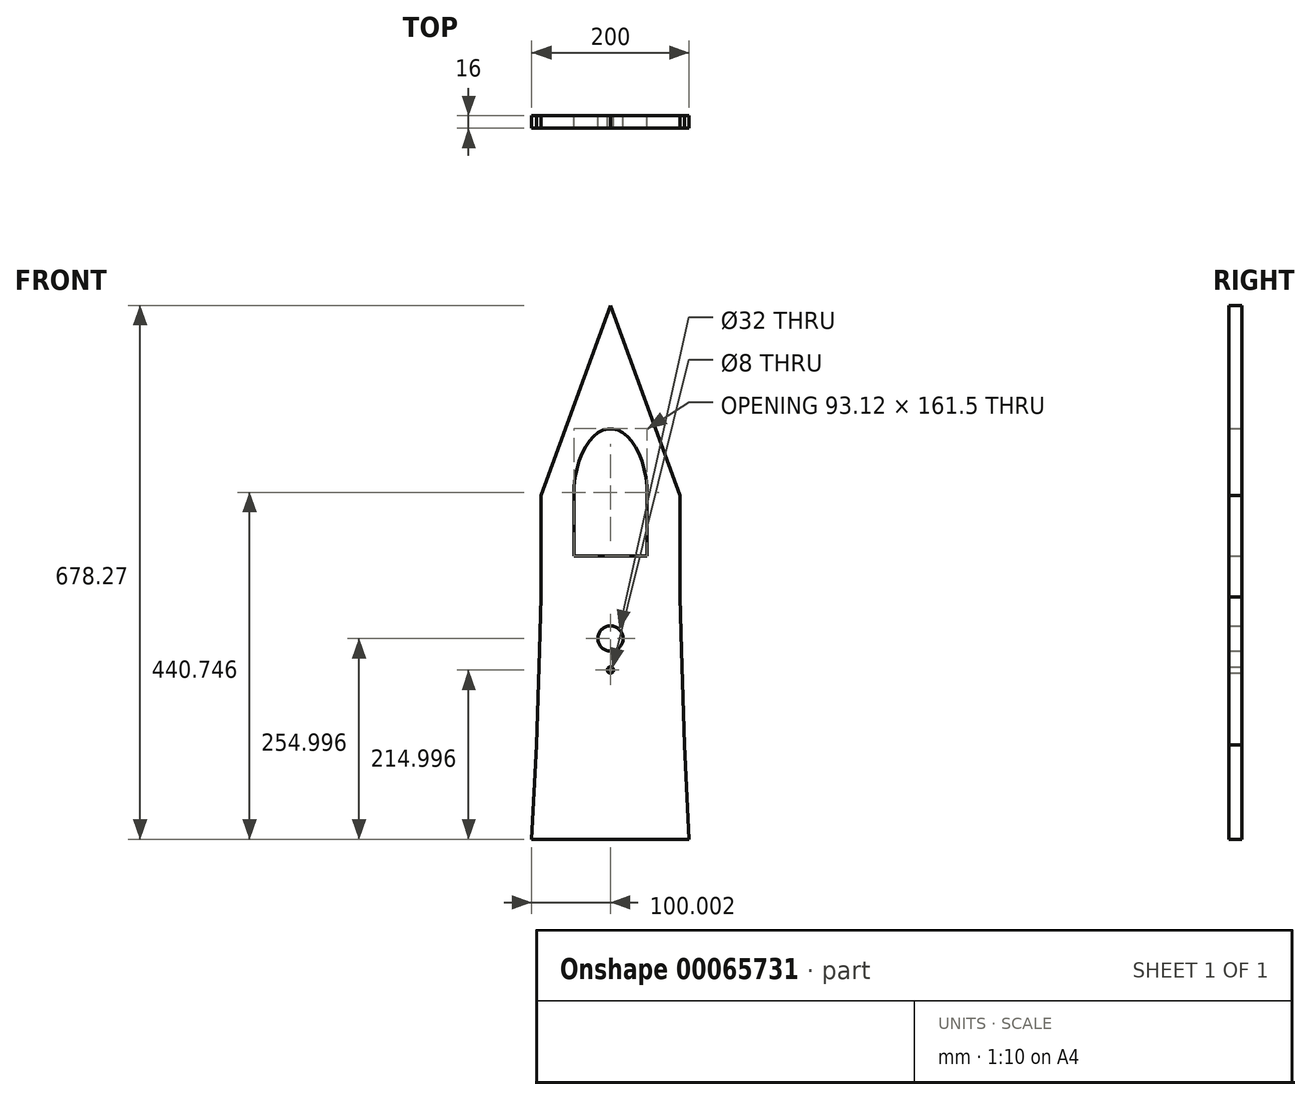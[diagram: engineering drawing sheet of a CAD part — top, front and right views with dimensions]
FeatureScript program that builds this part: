
annotation { "Feature Type Name" : "Feature", "Feature Type Description" : "" }
export const myFeature = defineFeature(function(context is Context, id is Id, definition is map)
    precondition{}
    {
        {
            var Q0;
            Q0=qCreatedBy(makeId("Front.planeOp"),FACE);
            var sketch = newSketch(context, id + "F0", { "sketchPlane" : qUnion([Q0])});
            skLineSegment(sketch, "E0.top", {"start": v(-7.07, -623.65) * mm, "end": v(-207.07, -623.65) * mm});
            skPoint(sketch, "E1.orphan", {"position": v(-214.14, 109.25) * mm});
            skPoint(sketch, "E2.orphan", {"position": v(0, 0) * mm});
            skLineSegment(sketch, "E3", {"start": v(-107.07, 54.62) * mm, "end": v(-107.07, -623.65) * mm, "construction": true});
            skCircle(sketch, "E4", {"center": v(-107.07, -368.65) * mm, "radius": 16 * mm});
            skCircle(sketch, "E5", {"center": v(-107.07, -408.65) * mm, "radius": 4 * mm});
            skLineSegment(sketch, "E6", {"start": v(-204.07, -563.65) * mm, "end": v(-10.07, -563.65) * mm, "construction": true});
            skLineSegment(sketch, "E7", {"start": v(-201.07, -503.65) * mm, "end": v(-13.07, -503.65) * mm, "construction": true});
            skLineSegment(sketch, "E8", {"start": v(-197.07, -383.65) * mm, "end": v(-17.07, -383.65) * mm, "construction": true});
            skLineSegment(sketch, "E9", {"start": v(-195.07, -315.65) * mm, "end": v(-19.07, -315.65) * mm, "construction": true});
            skLineSegment(sketch, "E10", {"start": v(-207.07, -623.65) * mm, "end": v(-204.07, -563.65) * mm});
            skLineSegment(sketch, "E11", {"start": v(-204.07, -563.65) * mm, "end": v(-201.07, -503.65) * mm});
            skLineSegment(sketch, "E12", {"start": v(-201.07, -503.65) * mm, "end": v(-197.07, -383.65) * mm});
            skLineSegment(sketch, "E13", {"start": v(-7.07, -623.65) * mm, "end": v(-10.07, -563.65) * mm});
            skLineSegment(sketch, "E14", {"start": v(-10.07, -563.65) * mm, "end": v(-13.07, -503.65) * mm});
            skLineSegment(sketch, "E15", {"start": v(-13.07, -503.65) * mm, "end": v(-17.07, -383.65) * mm});
            skLineSegment(sketch, "E16", {"start": v(-195.07, -315.65) * mm, "end": v(-197.07, -383.65) * mm});
            skLineSegment(sketch, "E17", {"start": v(-19.07, -315.65) * mm, "end": v(-17.07, -383.65) * mm});
            skLineSegment(sketch, "E18", {"start": v(-195.07, -315.65) * mm, "end": v(-195.07, -187.15) * mm});
            skLineSegment(sketch, "E19", {"start": v(-195.07, -187.15) * mm, "end": v(-19.07, -187.15) * mm, "construction": true});
            skLineSegment(sketch, "E20", {"start": v(-19.07, -187.15) * mm, "end": v(-19.07, -315.65) * mm});
            skLineSegment(sketch, "E21", {"start": v(-195.07, -187.15) * mm, "end": v(-107.07, 54.62) * mm});
            skLineSegment(sketch, "E22", {"start": v(-19.07, -187.15) * mm, "end": v(-107.07, 54.62) * mm});
            skLineSegment(sketch, "E23", {"start": v(-153.63, -263.65) * mm, "end": v(-60.5, -263.65) * mm});
            skEllipticalArc(sketch, "E24", {});
            skLineSegment(sketch, "E25", {"start": v(-153.63, -187.15) * mm, "end": v(-153.63, -263.65) * mm});
            skLineSegment(sketch, "E26", {"start": v(-60.5, -187.15) * mm, "end": v(-60.5, -263.65) * mm});
            const initialGuessF0  = {"E24": [-0.10706803202629114, -0.18715398755087015, 0, -1, 0.085, 0.04656, 1.5707963267948968, 4.71238898038469]};
            skSetInitialGuess(sketch, initialGuessF0);
            skSolve(sketch);
        }
        {
            var Q0;
            Q0 = qSketchRegion(id + "F0", true);
            extrude(context, id + "F1", {"entities" : qUnion([Q0]), "depth" : 16 * mm});
        }
    });
